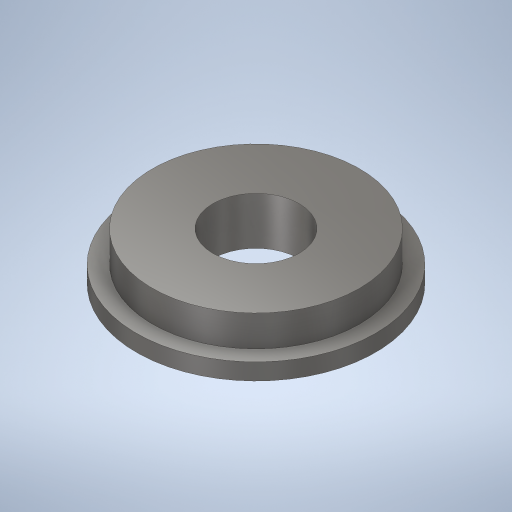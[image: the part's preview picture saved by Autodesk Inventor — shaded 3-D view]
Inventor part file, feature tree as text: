
AUTODESK INVENTOR PART (.ipt)
format: ipt  version: 2023.3 (Build 273359000, 359)  size: 260,096 bytes
history: native  units: in
note: dims shown in document units (in); Inventor stores cm internally (conversion verified against a paired STEP export)
features: sketch x3, extrude x2, hole x1
ambient origin geometry x8: Origin, YZ Plane, XZ Plane, XY Plane, X Axis, Y Axis, Z Axis, Center Point
bodies: Solid1 (feature_tree)
feature tree (6):
  extrude  "Extrusion1"  Depth=0.235in TaperAngle=0.0deg
  extrude  "Extrusion2"  Depth=0.175in TaperAngle=0.0deg
  hole  "Hole1"  [1 undecoded]
  sketch  "Sketch1"  dims[d0=0.865in d1=0.235in d2=0.0in]
  sketch  "Sketch2"  dims[d3=0.75in d4=0.175in d5=0.0in]
  sketch  "Sketch3"  dims[d6=0.3125in d7=0.75in d8=0.969in d9=0.0625in d10=0.5635in d11=1.0in d12=0.8108in]
note: 1 required parameter value undecoded (feature->parameter linkage not recoverable at this tier; creation-order binding heuristic only, values carry confidence <= 0.55)
